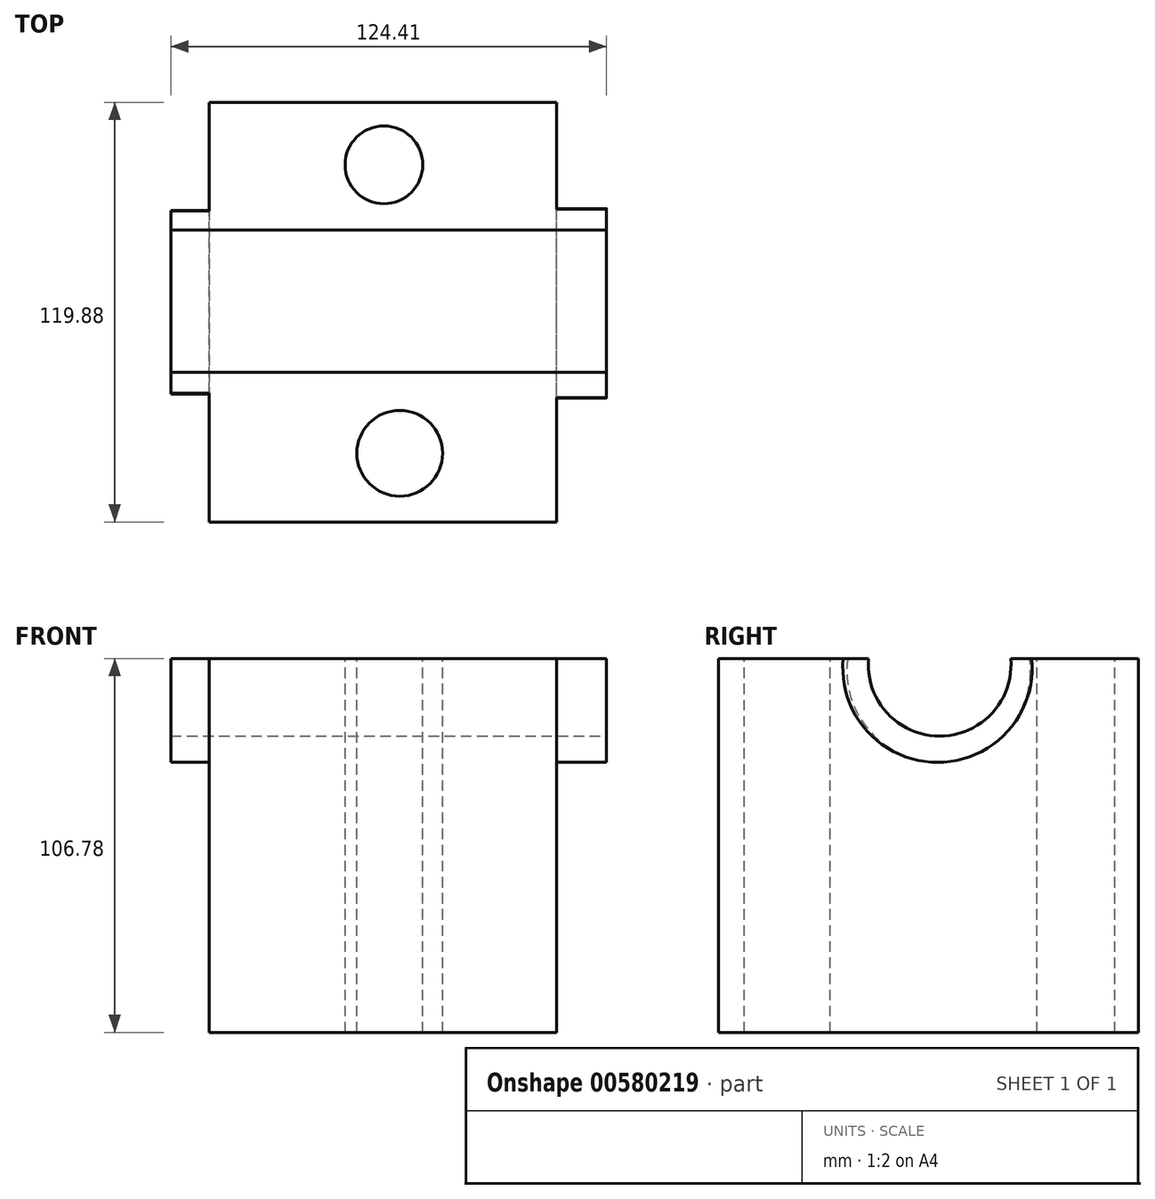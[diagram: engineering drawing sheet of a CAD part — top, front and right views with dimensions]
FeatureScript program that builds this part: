
annotation { "Feature Type Name" : "Feature", "Feature Type Description" : "" }
export const myFeature = defineFeature(function(context is Context, id is Id, definition is map)
    precondition{}
    {
        {
            var Q0;
            Q0=qCreatedBy(makeId("Front.planeOp"),FACE);
            var sketch = newSketch(context, id + "F0", { "sketchPlane" : qUnion([Q0])});
            skLineSegment(sketch, "E0.bottom", {"start": v(-44.22, 43.61) * mm, "end": v(55.04, 43.61) * mm});
            skLineSegment(sketch, "E0.top", {"start": v(-44.22, -63.17) * mm, "end": v(55.04, -63.17) * mm});
            skLineSegment(sketch, "E0.left", {"start": v(-44.22, 43.61) * mm, "end": v(-44.22, -63.17) * mm});
            skLineSegment(sketch, "E0.right", {"start": v(55.04, 43.61) * mm, "end": v(55.04, -63.17) * mm});
            skSolve(sketch);
        }
        {
            var Q0;
            Q0=makeQuery(id+"F0.imprint","IMPRINT",FACE,{"disambiguationData":[TD([[makeQuery(id+"F0.imprint","IMPRINT",EDGE,{"derivedFrom":sQuery(id+"F0.wireOp",EDGE,"E0.bottom")}),-1.0]])]});
            extrude(context, id + "F1", {"entities" : qUnion([Q0]), "endBound" : BoundingType.SYMMETRIC, "depth" : 119.89 * mm, "offsetDistance" : 25.4 * mm});
        }
        {
            var Q0;
            Q0=makeQuery(id+"F1.opExtrude","SWEPT_FACE",FACE,{"disambiguationData":[OSD([sQuery(id+"F0.wireOp",EDGE,"E0.right")])]});
            var sketch = newSketch(context, id + "F2", { "sketchPlane" : qUnion([Q0])});
            skArc(sketch, "E1", {"start": v(-17.15, 43.61) * mm, "mid": v(3.16, 21.46) * mm, "end": v(23.46, 43.61) * mm});
            skSolve(sketch);
        }
        {
            var Q0;
            {var subQ0=sQuery(id+"F2.wireOp",EDGE,"E1");Q0=makeQuery(id+"F2.imprint","IMPRINT",FACE,{"disambiguationData":[TD([[makeQuery(id+"F2.imprint","IMPRINT",EDGE,{"derivedFrom":subQ0}),1.0]])]});}
            extrude(context, id + "F3", {"entities" : qUnion([Q0]), "operationType" : NewBodyOperationType.REMOVE, "endBound" : BoundingType.THROUGH_ALL, "oppositeDirection" : true, "depth" : 25.4 * mm, "offsetDistance" : 25.4 * mm});
        }
        {
            var Q0;
            Q0=makeQuery(id+"F1.opExtrude","SWEPT_FACE",FACE,{"disambiguationData":[OSD([sQuery(id+"F0.wireOp",EDGE,"E0.right")])]});
            var sketch = newSketch(context, id + "F4", { "sketchPlane" : qUnion([Q0])});
            skArc(sketch, "E2", {"start": v(-24.36, 43.61) * mm, "mid": v(2.56, 13.94) * mm, "end": v(29.48, 43.61) * mm});
            skSolve(sketch);
        }
        {
            var Q0;
            {var subQ0=sQuery(id+"F4.wireOp",EDGE,"E2");Q0=makeQuery(id+"F4.imprint","IMPRINT",FACE,{"disambiguationData":[TD([[makeQuery(id+"F4.imprint","IMPRINT",EDGE,{"derivedFrom":subQ0}),1.0]])]});}
            extrude(context, id + "F5", {"entities" : qUnion([Q0]), "operationType" : NewBodyOperationType.ADD, "depth" : 14.22 * mm, "offsetDistance" : 25.4 * mm});
        }
        {
            var Q0;
            Q0=makeQuery(id+"F1.opExtrude","SWEPT_FACE",FACE,{"disambiguationData":[OSD([sQuery(id+"F0.wireOp",EDGE,"E0.left")])]});
            var sketch = newSketch(context, id + "F6", { "sketchPlane" : qUnion([Q0])});
            skArc(sketch, "E3", {"start": v(-28.88, 43.61) * mm, "mid": v(-2.86, 14.04) * mm, "end": v(23.16, 43.61) * mm});
            skSolve(sketch);
        }
        {
            var Q0;
            {var subQ0=sQuery(id+"F6.wireOp",EDGE,"E3");Q0=makeQuery(id+"F6.imprint","IMPRINT",FACE,{"disambiguationData":[TD([[makeQuery(id+"F6.imprint","IMPRINT",EDGE,{"derivedFrom":subQ0}),1.0]])]});}
            extrude(context, id + "F7", {"entities" : qUnion([Q0]), "operationType" : NewBodyOperationType.ADD, "depth" : 10.92 * mm, "offsetDistance" : 25.4 * mm});
        }
        {
            var Q0;
            {var subQ0=sQuery(id+"F0.wireOp",EDGE,"E0.bottom");var subQ1=makeQuery(id+"F1.opExtrude","SWEPT_FACE",FACE,{"disambiguationData":[OSD([subQ0])]});var subQ2=sQuery(id+"F0.wireOp",EDGE,"E0.right");var subQ3=sQuery(id+"F0.wireOp",EDGE,"E0.left");var subQ4=makeQuery(id+"F1.opExtrude","CAP_FACE",FACE,{"disambiguationData":[OSD([subQ0,sQuery(id+"F0.wireOp",EDGE,"E0.top"),subQ3,subQ2])],"isStart":true});var subQ6=sQuery(id+"F2.wireOp",EDGE,"E1");var subQ8=makeQuery(id+"F3.boolean.opBoolean","SPLIT",EDGE,{"disambiguationData":[TD([subQ4])],"derivedFrom":makeQuery(id+"F1.opExtrude","SWEPT_EDGE",EDGE,{"disambiguationData":[OSD([subQ0,subQ3])]})});var subQ10=makeQuery(id+"F3.boolean.opBoolean","SPLIT",EDGE,{"disambiguationData":[TD([subQ4])],"derivedFrom":makeQuery(id+"F1.opExtrude","SWEPT_EDGE",EDGE,{"disambiguationData":[OSD([subQ0,subQ2])]})});Q0=makeQuery(id+"F7.boolean.opBoolean","MERGE",FACE,{"derivedFrom":[makeQuery(id+"F5.boolean.opBoolean","MERGE",FACE,{"derivedFrom":[makeQuery(id+"F3.boolean.opBoolean","SPLIT",FACE,{"disambiguationData":[TD([subQ4])],"derivedFrom":subQ1}),makeQuery(id+"F5.opExtrude","SWEPT_FACE",FACE,{"disambiguationData":[OSD([subQ0,subQ2]),TDD([makeQuery(id+"F4.imprint","IMPRINT",EDGE,{"disambiguationData":[TD([[makeQuery(id+"F4.imprint","INTERSECT",VERTEX,{"derivedFrom":[makeQuery(id+"F3.boolean.opBoolean","COPY",EDGE,{"derivedFrom":makeQuery(id+"F3.opExtrude","CAP_EDGE",EDGE,{"disambiguationData":[OSD([subQ6])],"isStart":true})}),subQ10]}),-1.0]])],"derivedFrom":subQ10})])]})]}),makeQuery(id+"F7.opExtrude","SWEPT_FACE",FACE,{"disambiguationData":[OSD([subQ0,subQ3]),TDD([makeQuery(id+"F6.imprint","IMPRINT",EDGE,{"disambiguationData":[TD([[makeQuery(id+"F6.imprint","INTERSECT",VERTEX,{"derivedFrom":[subQ8,sQuery(id+"F6.wireOp",EDGE,"E3")]}),1.0]])],"derivedFrom":subQ8})])]})]});}
            var sketch = newSketch(context, id + "F8", { "sketchPlane" : qUnion([Q0])});
            skCircle(sketch, "E4", {"center": v(5.72, 42.11) * mm, "radius": 11.1 * mm});
            skCircle(sketch, "E5", {"center": v(10.23, -40.3) * mm, "radius": 12.24 * mm});
            skSolve(sketch);
        }
        {
            var Q0;
            Q0=makeQuery(id+"F8.imprint","IMPRINT",FACE,{"disambiguationData":[TD([[makeQuery(id+"F8.imprint","IMPRINT",EDGE,{"derivedFrom":sQuery(id+"F8.wireOp",EDGE,"E4")}),1.0]])]});
            var Q1;
            Q1=makeQuery(id+"F8.imprint","IMPRINT",FACE,{"disambiguationData":[TD([[makeQuery(id+"F8.imprint","IMPRINT",EDGE,{"derivedFrom":sQuery(id+"F8.wireOp",EDGE,"E5")}),1.0]])]});
            extrude(context, id + "F9", {"entities" : qUnion([Q0, Q1]), "operationType" : NewBodyOperationType.REMOVE, "endBound" : BoundingType.THROUGH_ALL, "oppositeDirection" : true, "depth" : 25.4 * mm, "offsetDistance" : 25.4 * mm});
        }
    });
